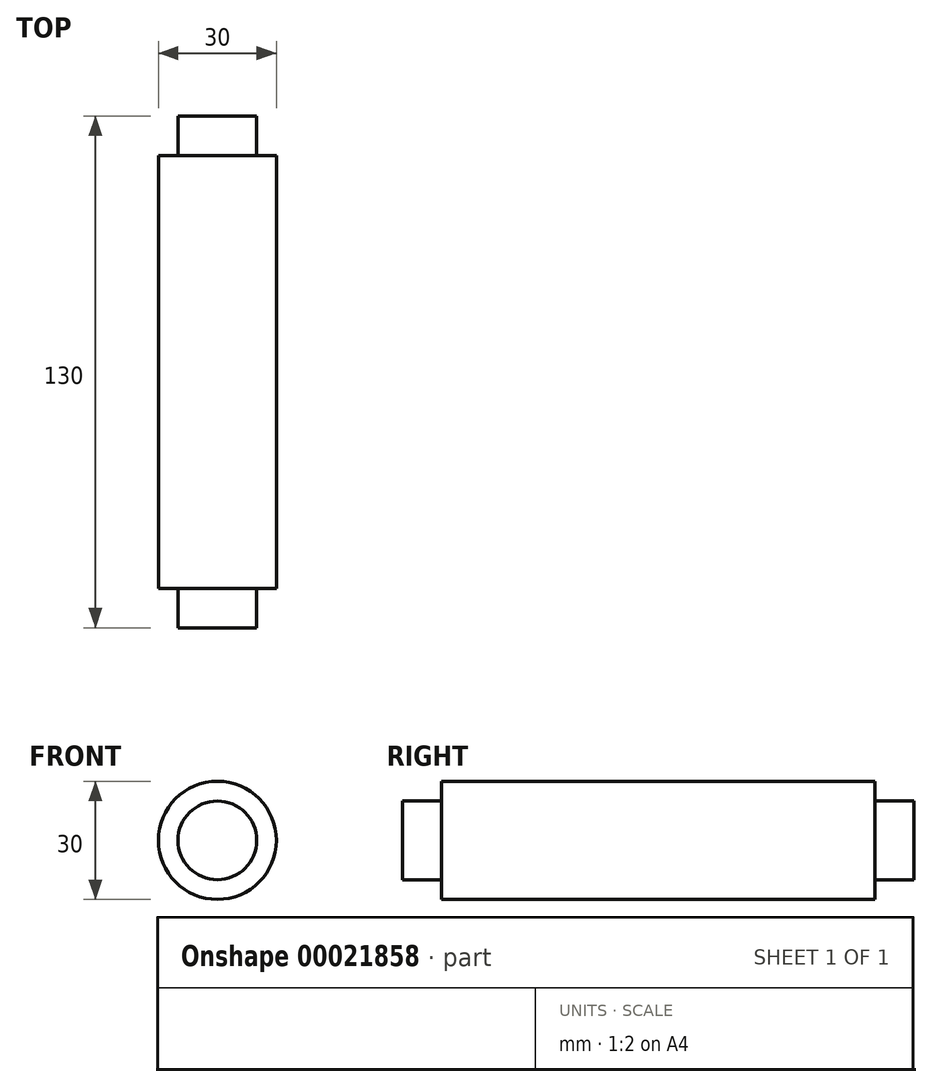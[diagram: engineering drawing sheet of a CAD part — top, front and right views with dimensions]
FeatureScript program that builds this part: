
annotation { "Feature Type Name" : "Feature", "Feature Type Description" : "" }
export const myFeature = defineFeature(function(context is Context, id is Id, definition is map)
    precondition{}
    {
        {
            var Q0;
            Q0=qCreatedBy(makeId("Front.planeOp"),FACE);
            var sketch = newSketch(context, id + "F0", { "sketchPlane" : qUnion([Q0])});
            skCircle(sketch, "E0", {"center": v(0, 0) * mm, "radius": 15 * mm});
            skSolve(sketch);
        }
        {
            var Q0;
            Q0=makeQuery(id+"F0.imprint","IMPRINT",FACE,{"disambiguationData":[TD([[makeQuery(id+"F0.imprint","IMPRINT",EDGE,{"derivedFrom":sQuery(id+"F0.wireOp",EDGE,"E0")}),1.0]])]});
            extrude(context, id + "F1", {"entities" : qUnion([Q0]), "depth" : 110 * mm});
        }
        {
            var Q0;
            Q0=makeQuery(id+"F1.opExtrude","CAP_FACE",FACE,{"disambiguationData":[OSD([sQuery(id+"F0.wireOp",EDGE,"E0")])],"isStart":false});
            var sketch = newSketch(context, id + "F2", { "sketchPlane" : qUnion([Q0])});
            skCircle(sketch, "E1", {"center": v(0, 0) * mm, "radius": 10 * mm});
            skSolve(sketch);
        }
        {
            var Q0;
            Q0=makeQuery(id+"F2.imprint","IMPRINT",FACE,{"disambiguationData":[TD([[makeQuery(id+"F2.imprint","IMPRINT",EDGE,{"derivedFrom":sQuery(id+"F2.wireOp",EDGE,"E1")}),1.0]])]});
            extrude(context, id + "F3", {"entities" : qUnion([Q0]), "operationType" : NewBodyOperationType.ADD, "depth" : 10 * mm});
        }
        {
            var Q0;
            Q0=makeQuery(id+"F1.opExtrude","CAP_FACE",FACE,{"disambiguationData":[OSD([sQuery(id+"F0.wireOp",EDGE,"E0")])],"isStart":true});
            var sketch = newSketch(context, id + "F4", { "sketchPlane" : qUnion([Q0])});
            skCircle(sketch, "E2", {"center": v(0, 0) * mm, "radius": 10 * mm});
            skSolve(sketch);
        }
        {
            var Q0;
            Q0=makeQuery(id+"F4.imprint","IMPRINT",FACE,{"disambiguationData":[TD([[makeQuery(id+"F4.imprint","IMPRINT",EDGE,{"derivedFrom":sQuery(id+"F4.wireOp",EDGE,"E2")}),1.0]])]});
            extrude(context, id + "F5", {"entities" : qUnion([Q0]), "operationType" : NewBodyOperationType.ADD, "depth" : 10 * mm});
        }
    });
